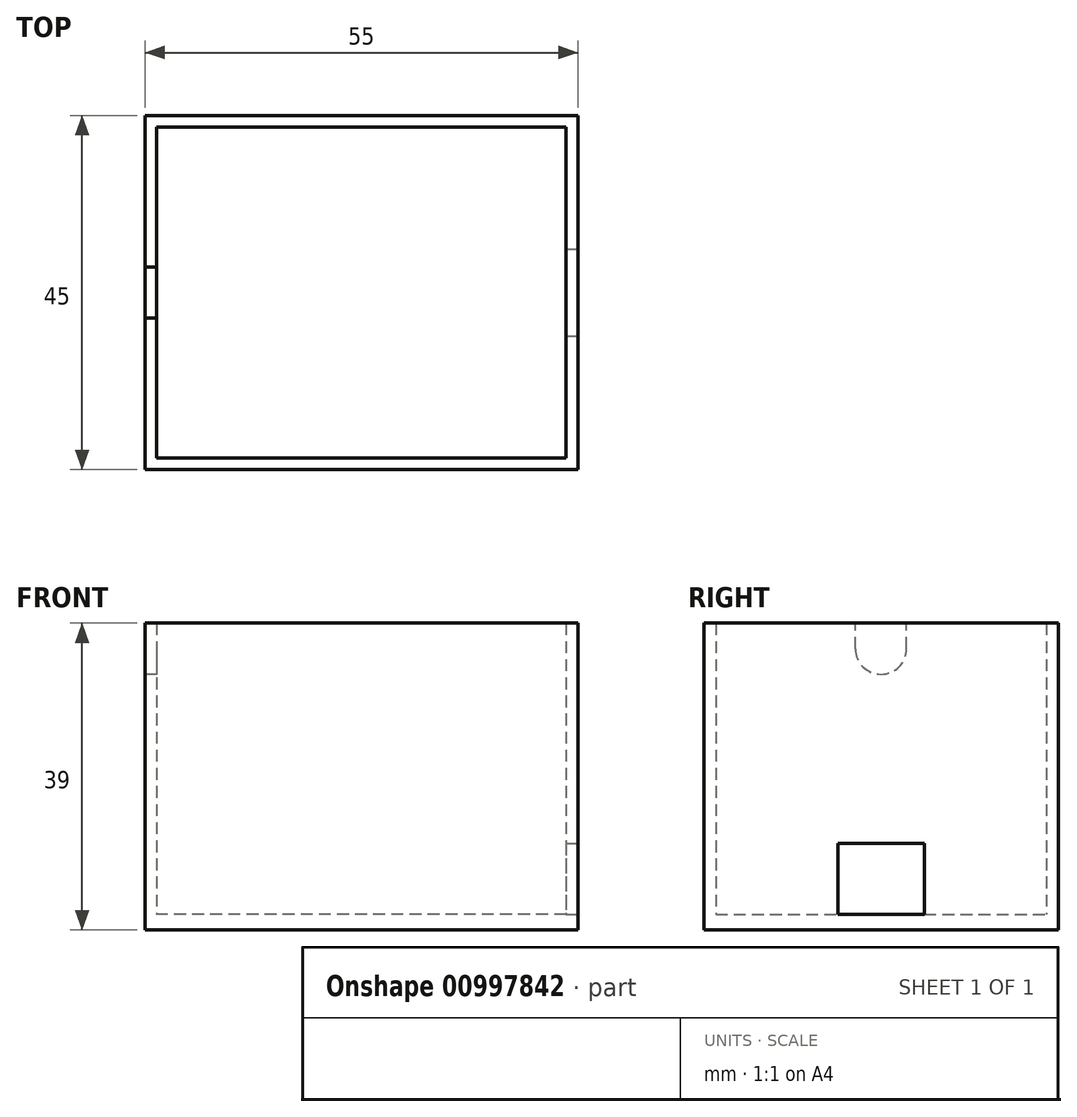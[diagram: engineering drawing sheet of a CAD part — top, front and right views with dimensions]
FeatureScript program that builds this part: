
annotation { "Feature Type Name" : "Feature", "Feature Type Description" : "" }
export const myFeature = defineFeature(function(context is Context, id is Id, definition is map)
    precondition{}
    {
        {
            var Q0;
            Q0=qCreatedBy(makeId("Top.planeOp"),FACE);
            var sketch = newSketch(context, id + "F0", { "sketchPlane" : qUnion([Q0])});
            skLineSegment(sketch, "E0.bottom", {"start": v(0, 0) * mm, "end": v(55, 0) * mm});
            skLineSegment(sketch, "E0.top", {"start": v(0, 45) * mm, "end": v(55, 45) * mm});
            skLineSegment(sketch, "E0.left", {"start": v(0, 0) * mm, "end": v(0, 45) * mm});
            skLineSegment(sketch, "E0.right", {"start": v(55, 0) * mm, "end": v(55, 45) * mm});
            skSolve(sketch);
        }
        {
            var Q0;
            Q0 = qSketchRegion(id + "F0", true);
            extrude(context, id + "F1", {"entities" : qUnion([Q0]), "depth" : 2 * mm, "offsetDistance" : 25 * mm});
        }
        {
            var Q0;
            Q0=makeQuery(id+"F1.opExtrude","CAP_FACE",FACE,{"disambiguationData":[OSD([sQuery(id+"F0.wireOp",EDGE,"E0.bottom"),sQuery(id+"F0.wireOp",EDGE,"E0.top"),sQuery(id+"F0.wireOp",EDGE,"E0.left"),sQuery(id+"F0.wireOp",EDGE,"E0.right")])],"isStart":false});
            var sketch = newSketch(context, id + "F2", { "sketchPlane" : qUnion([Q0])});
            skLineSegment(sketch, "E1.0", {"start": v(53.5, 43.5) * mm, "end": v(1.5, 43.5) * mm});
            skLineSegment(sketch, "E1.1", {"start": v(53.5, 1.5) * mm, "end": v(53.5, 43.5) * mm});
            skLineSegment(sketch, "E1.2", {"start": v(1.5, 1.5) * mm, "end": v(53.5, 1.5) * mm});
            skLineSegment(sketch, "E1.3", {"start": v(1.5, 43.5) * mm, "end": v(1.5, 1.5) * mm});
            skSolve(sketch);
        }
        {
            var Q0;
            Q0=makeQuery(id+"F2.imprint","IMPRINT",FACE,{"disambiguationData":[TD([[makeQuery(id+"F2.imprint","IMPRINT",EDGE,{"derivedFrom":sQuery(id+"F2.wireOp",EDGE,"E1.0")}),-1.0]])]});
            extrude(context, id + "F3", {"entities" : qUnion([Q0]), "operationType" : NewBodyOperationType.ADD, "depth" : 37 * mm, "offsetDistance" : 25 * mm});
        }
        {
            var Q0;
            {var subQ0=sQuery(id+"F0.wireOp",EDGE,"E0.left");Q0=makeQuery(id+"F3.boolean.opBoolean","MERGE",FACE,{"derivedFrom":[makeQuery(id+"F1.opExtrude","SWEPT_FACE",FACE,{"disambiguationData":[OSD([subQ0])]}),makeQuery(id+"F3.opExtrude","SWEPT_FACE",FACE,{"disambiguationData":[OSD([subQ0])]})]});}
            var sketch = newSketch(context, id + "F4", { "sketchPlane" : qUnion([Q0])});
            skArc(sketch, "E2", {"start": v(-25.75, 35.75) * mm, "mid": v(-22.5, 32.5) * mm, "end": v(-19.25, 35.75) * mm});
            skLineSegment(sketch, "E3", {"start": v(-25.75, 35.75) * mm, "end": v(-25.75, 39) * mm});
            skLineSegment(sketch, "E4", {"start": v(-19.25, 35.75) * mm, "end": v(-19.25, 39) * mm});
            skLineSegment(sketch, "E5", {"start": v(-25.75, 39) * mm, "end": v(-19.25, 39) * mm});
            skSolve(sketch);
        }
        {
            var Q0;
            Q0=makeQuery(id+"F4.imprint","IMPRINT",FACE,{"disambiguationData":[TD([[makeQuery(id+"F4.imprint","IMPRINT",EDGE,{"derivedFrom":sQuery(id+"F4.wireOp",EDGE,"E2")}),1.0]])]});
            extrude(context, id + "F5", {"entities" : qUnion([Q0]), "operationType" : NewBodyOperationType.REMOVE, "oppositeDirection" : true, "depth" : 25 * mm, "offsetDistance" : 25 * mm});
        }
        {
            var Q0;
            {var subQ0=sQuery(id+"F0.wireOp",EDGE,"E0.right");Q0=makeQuery(id+"F3.boolean.opBoolean","MERGE",FACE,{"derivedFrom":[makeQuery(id+"F1.opExtrude","SWEPT_FACE",FACE,{"disambiguationData":[OSD([subQ0])]}),makeQuery(id+"F3.opExtrude","SWEPT_FACE",FACE,{"disambiguationData":[OSD([subQ0])]})]});}
            var sketch = newSketch(context, id + "F6", { "sketchPlane" : qUnion([Q0])});
            skLineSegment(sketch, "E6.top", {"start": v(22.5, 0) * mm, "end": v(22.5, 0) * mm});
            skLineSegment(sketch, "E7.bottom", {"start": v(17, 0) * mm, "end": v(28, 0) * mm});
            skLineSegment(sketch, "E7.top", {"start": v(17, 2) * mm, "end": v(28, 2) * mm});
            skLineSegment(sketch, "E7.left", {"start": v(17, 0) * mm, "end": v(17, 2) * mm});
            skLineSegment(sketch, "E7.right", {"start": v(28, 0) * mm, "end": v(28, 2) * mm});
            skLineSegment(sketch, "E8.top", {"start": v(17, 11) * mm, "end": v(28, 11) * mm});
            skLineSegment(sketch, "E8.left", {"start": v(17, 2) * mm, "end": v(17, 11) * mm});
            skLineSegment(sketch, "E8.right", {"start": v(28, 2) * mm, "end": v(28, 11) * mm});
            skSolve(sketch);
        }
        {
            var Q0;
            Q0=makeQuery(id+"F6.imprint","IMPRINT",FACE,{"disambiguationData":[TD([[makeQuery(id+"F6.imprint","IMPRINT",EDGE,{"derivedFrom":sQuery(id+"F6.wireOp",EDGE,"E7.top")}),1.0]])]});
            extrude(context, id + "F7", {"entities" : qUnion([Q0]), "operationType" : NewBodyOperationType.REMOVE, "oppositeDirection" : true, "depth" : 25 * mm, "offsetDistance" : 25 * mm});
        }
    });
